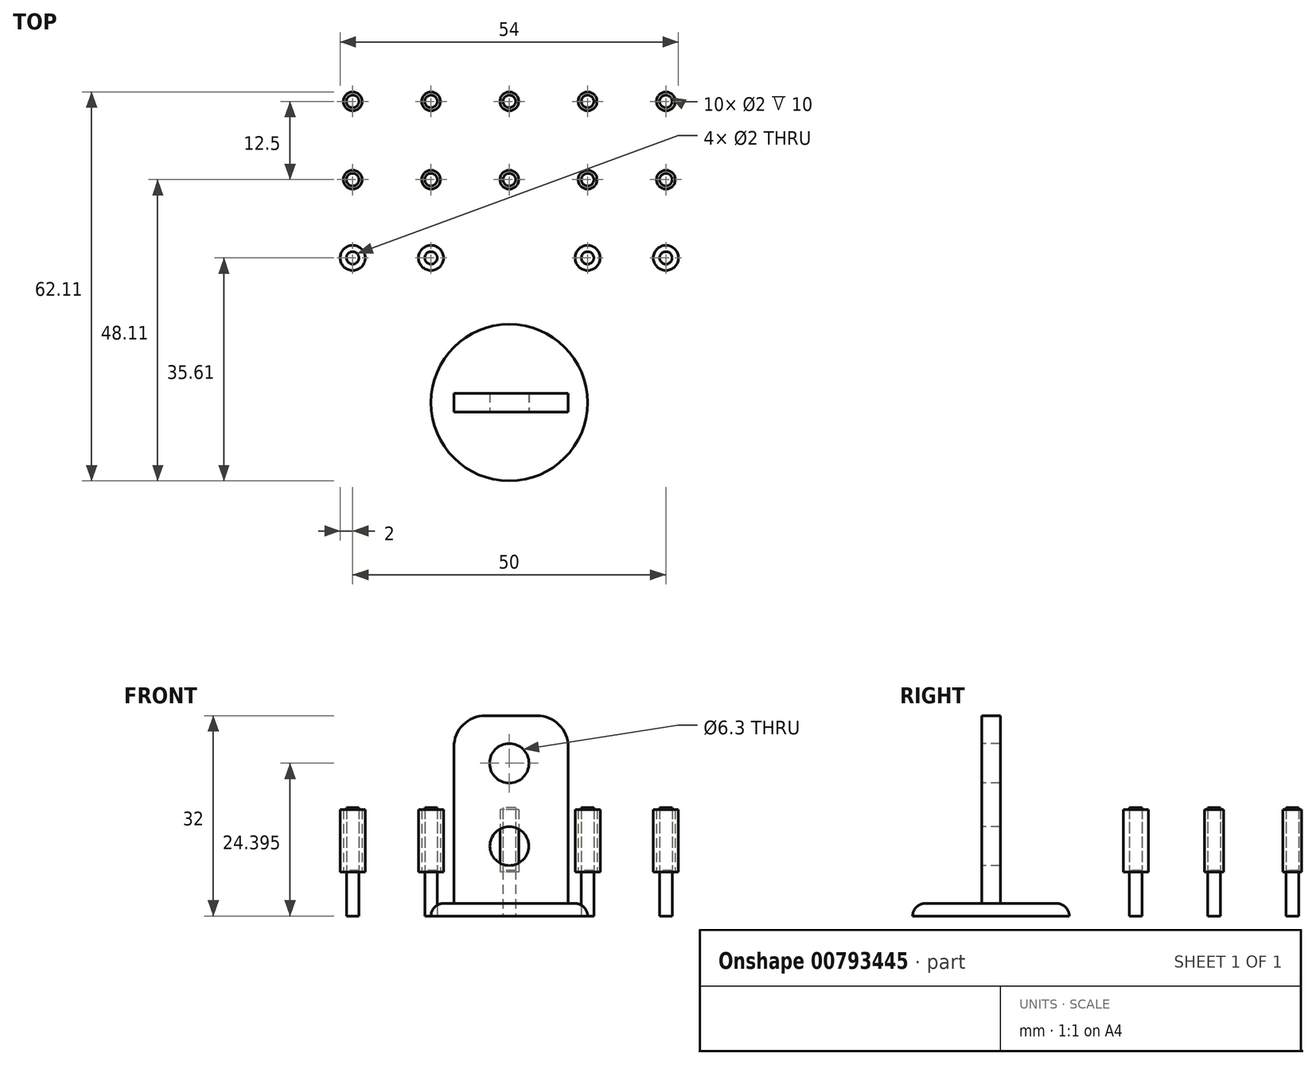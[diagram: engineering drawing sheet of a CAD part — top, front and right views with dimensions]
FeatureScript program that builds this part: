
annotation { "Feature Type Name" : "Feature", "Feature Type Description" : "" }
export const myFeature = defineFeature(function(context is Context, id is Id, definition is map)
    precondition{}
    {
        {
            var Q0;
            Q0=qCreatedBy(makeId("Top.planeOp"),FACE);
            var sketch = newSketch(context, id + "F0", { "sketchPlane" : qUnion([Q0])});
            skPoint(sketch, "E0.middle", {"position": v(0, 0) * mm});
            skCircle(sketch, "E1", {"center": v(-12.5, 25) * mm, "radius": 1 * mm});
            skCircle(sketch, "E2", {"center": v(0, 25) * mm, "radius": 1 * mm});
            skCircle(sketch, "E3", {"center": v(12.5, 25) * mm, "radius": 1 * mm});
            skCircle(sketch, "E4", {"center": v(25, 25) * mm, "radius": 1 * mm});
            skCircle(sketch, "E5", {"center": v(-25, 25) * mm, "radius": 1 * mm});
            skCircle(sketch, "E6", {"center": v(-25, 12.5) * mm, "radius": 1 * mm});
            skCircle(sketch, "E7", {"center": v(-12.5, 12.5) * mm, "radius": 1 * mm});
            skCircle(sketch, "E8", {"center": v(0, 12.5) * mm, "radius": 1 * mm});
            skCircle(sketch, "E9", {"center": v(12.5, 12.5) * mm, "radius": 1 * mm});
            skCircle(sketch, "E10", {"center": v(25, 12.5) * mm, "radius": 1 * mm});
            skCircle(sketch, "E11", {"center": v(-25, 0) * mm, "radius": 1 * mm});
            skCircle(sketch, "E12", {"center": v(-12.5, 0) * mm, "radius": 1 * mm});
            skCircle(sketch, "E13", {"center": v(12.5, 0) * mm, "radius": 1 * mm});
            skCircle(sketch, "E14", {"center": v(25, 0) * mm, "radius": 1 * mm});
            skSolve(sketch);
        }
        {
            var Q0;
            Q0=makeQuery(id+"F0.imprint","IMPRINT",FACE,{"disambiguationData":[TD([[makeQuery(id+"F0.imprint","IMPRINT",EDGE,{"derivedFrom":sQuery(id+"F0.wireOp",EDGE,"E5")}),1.0]])]});
            var Q1;
            Q1=makeQuery(id+"F0.imprint","IMPRINT",FACE,{"disambiguationData":[TD([[makeQuery(id+"F0.imprint","IMPRINT",EDGE,{"derivedFrom":sQuery(id+"F0.wireOp",EDGE,"E1")}),1.0]])]});
            var Q2;
            Q2=makeQuery(id+"F0.imprint","IMPRINT",FACE,{"disambiguationData":[TD([[makeQuery(id+"F0.imprint","IMPRINT",EDGE,{"derivedFrom":sQuery(id+"F0.wireOp",EDGE,"E6")}),1.0]])]});
            var Q3;
            Q3=makeQuery(id+"F0.imprint","IMPRINT",FACE,{"disambiguationData":[TD([[makeQuery(id+"F0.imprint","IMPRINT",EDGE,{"derivedFrom":sQuery(id+"F0.wireOp",EDGE,"E7")}),1.0]])]});
            var Q4;
            Q4=makeQuery(id+"F0.imprint","IMPRINT",FACE,{"disambiguationData":[TD([[makeQuery(id+"F0.imprint","IMPRINT",EDGE,{"derivedFrom":sQuery(id+"F0.wireOp",EDGE,"E2")}),1.0]])]});
            var Q5;
            Q5=makeQuery(id+"F0.imprint","IMPRINT",FACE,{"disambiguationData":[TD([[makeQuery(id+"F0.imprint","IMPRINT",EDGE,{"derivedFrom":sQuery(id+"F0.wireOp",EDGE,"E3")}),1.0]])]});
            var Q6;
            Q6=makeQuery(id+"F0.imprint","IMPRINT",FACE,{"disambiguationData":[TD([[makeQuery(id+"F0.imprint","IMPRINT",EDGE,{"derivedFrom":sQuery(id+"F0.wireOp",EDGE,"E8")}),1.0]])]});
            var Q7;
            Q7=makeQuery(id+"F0.imprint","IMPRINT",FACE,{"disambiguationData":[TD([[makeQuery(id+"F0.imprint","IMPRINT",EDGE,{"derivedFrom":sQuery(id+"F0.wireOp",EDGE,"E9")}),1.0]])]});
            var Q8;
            Q8=makeQuery(id+"F0.imprint","IMPRINT",FACE,{"disambiguationData":[TD([[makeQuery(id+"F0.imprint","IMPRINT",EDGE,{"derivedFrom":sQuery(id+"F0.wireOp",EDGE,"E4")}),1.0]])]});
            var Q9;
            Q9=makeQuery(id+"F0.imprint","IMPRINT",FACE,{"disambiguationData":[TD([[makeQuery(id+"F0.imprint","IMPRINT",EDGE,{"derivedFrom":sQuery(id+"F0.wireOp",EDGE,"E10")}),1.0]])]});
            var Q10;
            Q10=makeQuery(id+"F0.imprint","IMPRINT",FACE,{"disambiguationData":[TD([[makeQuery(id+"F0.imprint","IMPRINT",EDGE,{"derivedFrom":sQuery(id+"F0.wireOp",EDGE,"E14")}),1.0]])]});
            var Q11;
            Q11=makeQuery(id+"F0.imprint","IMPRINT",FACE,{"disambiguationData":[TD([[makeQuery(id+"F0.imprint","IMPRINT",EDGE,{"derivedFrom":sQuery(id+"F0.wireOp",EDGE,"E13")}),1.0]])]});
            var Q12;
            Q12=makeQuery(id+"F0.imprint","IMPRINT",FACE,{"disambiguationData":[TD([[makeQuery(id+"F0.imprint","IMPRINT",EDGE,{"derivedFrom":sQuery(id+"F0.wireOp",EDGE,"E12")}),1.0]])]});
            var Q13;
            Q13=makeQuery(id+"F0.imprint","IMPRINT",FACE,{"disambiguationData":[TD([[makeQuery(id+"F0.imprint","IMPRINT",EDGE,{"derivedFrom":sQuery(id+"F0.wireOp",EDGE,"E11")}),1.0]])]});
            extrude(context, id + "F1", {"entities" : qUnion([Q0, Q1, Q2, Q3, Q4, Q5, Q6, Q7, Q8, Q9, Q10, Q11, Q12, Q13]), "depth" : 7.3 * mm, "offsetDistance" : 25 * mm});
        }
        {
            var Q0;
            Q0=qCreatedBy(makeId("Top.planeOp"),FACE);
            cPlane(context, id + "F2", {"entities" : qUnion([Q0]), "cplaneType" : CPlaneType.OFFSET, "offset" : 7 * mm, "width" : 150 * mm, "height" : 150 * mm});
        }
        {
            var Q0;
            Q0=qCreatedBy(id+"F2.planeOp",FACE);
            var sketch = newSketch(context, id + "F3", { "sketchPlane" : qUnion([Q0])});
            skCircle(sketch, "E15.0.0", {"center": v(-25, 25) * mm, "radius": 1 * mm});
            skCircle(sketch, "E16.0.0", {"center": v(-12.5, 25) * mm, "radius": 1 * mm});
            skCircle(sketch, "E17.0.0", {"center": v(0, 25) * mm, "radius": 1 * mm});
            skCircle(sketch, "E18.0.0", {"center": v(-12.5, 12.5) * mm, "radius": 1 * mm});
            skCircle(sketch, "E19.0.0", {"center": v(-25, 12.5) * mm, "radius": 1 * mm});
            skCircle(sketch, "E20.0.0", {"center": v(0, 12.5) * mm, "radius": 1 * mm});
            skCircle(sketch, "E21.0.0", {"center": v(12.5, 25) * mm, "radius": 1 * mm});
            skCircle(sketch, "E22.0.0", {"center": v(12.5, 12.5) * mm, "radius": 1 * mm});
            skCircle(sketch, "E23.0.0", {"center": v(25, 12.5) * mm, "radius": 1 * mm});
            skCircle(sketch, "E24.0.0", {"center": v(25, 25) * mm, "radius": 1 * mm});
            skCircle(sketch, "E25.0.0", {"center": v(25, 0) * mm, "radius": 1 * mm});
            skCircle(sketch, "E26.0.0", {"center": v(12.5, 0) * mm, "radius": 1 * mm});
            skCircle(sketch, "E27.0.0", {"center": v(-12.5, 0) * mm, "radius": 1 * mm});
            skCircle(sketch, "E28.0.0", {"center": v(-25, 0) * mm, "radius": 1 * mm});
            skCircle(sketch, "E29", {"center": v(-25, 25) * mm, "radius": 1.5 * mm});
            skCircle(sketch, "E30", {"center": v(-12.5, 25) * mm, "radius": 1.5 * mm});
            skCircle(sketch, "E31", {"center": v(0, 25) * mm, "radius": 1.5 * mm});
            skCircle(sketch, "E32", {"center": v(12.5, 25) * mm, "radius": 1.5 * mm});
            skCircle(sketch, "E33", {"center": v(25, 25) * mm, "radius": 1.5 * mm});
            skCircle(sketch, "E34", {"center": v(-25, 12.5) * mm, "radius": 1.5 * mm});
            skCircle(sketch, "E35", {"center": v(-12.5, 12.5) * mm, "radius": 1.5 * mm});
            skCircle(sketch, "E36", {"center": v(0, 12.5) * mm, "radius": 1.5 * mm});
            skCircle(sketch, "E37", {"center": v(12.5, 12.5) * mm, "radius": 1.5 * mm});
            skCircle(sketch, "E38", {"center": v(25, 12.5) * mm, "radius": 1.5 * mm});
            skCircle(sketch, "E39", {"center": v(-25, 0) * mm, "radius": 2 * mm});
            skCircle(sketch, "E40", {"center": v(-12.5, 0) * mm, "radius": 2 * mm});
            skCircle(sketch, "E41", {"center": v(12.5, 0) * mm, "radius": 2 * mm});
            skCircle(sketch, "E42", {"center": v(25, 0) * mm, "radius": 2 * mm});
            skSolve(sketch);
        }
        {
            var Q0;
            Q0=makeQuery(id+"F3.imprint","IMPRINT",FACE,{"disambiguationData":[TD([[makeQuery(id+"F3.imprint","IMPRINT",EDGE,{"derivedFrom":sQuery(id+"F3.wireOp",EDGE,"E19.0.0")}),-1.0]])]});
            var Q1;
            Q1=makeQuery(id+"F1.opExtrude","CAP_FACE",FACE,{"disambiguationData":[OSD([sQuery(id+"F0.wireOp",EDGE,"E6")])],"isStart":false});
            var Q2;
            Q2=makeQuery(id+"F3.imprint","IMPRINT",FACE,{"disambiguationData":[TD([[makeQuery(id+"F3.imprint","IMPRINT",EDGE,{"derivedFrom":sQuery(id+"F3.wireOp",EDGE,"E28.0.0")}),-1.0]])]});
            var Q3;
            Q3=makeQuery(id+"F1.opExtrude","CAP_FACE",FACE,{"disambiguationData":[OSD([sQuery(id+"F0.wireOp",EDGE,"E11")])],"isStart":false});
            var Q4;
            Q4=makeQuery(id+"F3.imprint","IMPRINT",FACE,{"disambiguationData":[TD([[makeQuery(id+"F3.imprint","IMPRINT",EDGE,{"derivedFrom":sQuery(id+"F3.wireOp",EDGE,"E27.0.0")}),-1.0]])]});
            var Q5;
            Q5=makeQuery(id+"F1.opExtrude","CAP_FACE",FACE,{"disambiguationData":[OSD([sQuery(id+"F0.wireOp",EDGE,"E12")])],"isStart":false});
            var Q6;
            Q6=makeQuery(id+"F3.imprint","IMPRINT",FACE,{"disambiguationData":[TD([[makeQuery(id+"F3.imprint","IMPRINT",EDGE,{"derivedFrom":sQuery(id+"F3.wireOp",EDGE,"E18.0.0")}),-1.0]])]});
            var Q7;
            Q7=makeQuery(id+"F1.opExtrude","CAP_FACE",FACE,{"disambiguationData":[OSD([sQuery(id+"F0.wireOp",EDGE,"E7")])],"isStart":false});
            var Q8;
            Q8=makeQuery(id+"F3.imprint","IMPRINT",FACE,{"disambiguationData":[TD([[makeQuery(id+"F3.imprint","IMPRINT",EDGE,{"derivedFrom":sQuery(id+"F3.wireOp",EDGE,"E15.0.0")}),-1.0]])]});
            var Q9;
            Q9=makeQuery(id+"F1.opExtrude","CAP_FACE",FACE,{"disambiguationData":[OSD([sQuery(id+"F0.wireOp",EDGE,"E5")])],"isStart":false});
            var Q10;
            Q10=makeQuery(id+"F3.imprint","IMPRINT",FACE,{"disambiguationData":[TD([[makeQuery(id+"F3.imprint","IMPRINT",EDGE,{"derivedFrom":sQuery(id+"F3.wireOp",EDGE,"E16.0.0")}),-1.0]])]});
            var Q11;
            Q11=makeQuery(id+"F1.opExtrude","CAP_FACE",FACE,{"disambiguationData":[OSD([sQuery(id+"F0.wireOp",EDGE,"E1")])],"isStart":false});
            var Q12;
            Q12=makeQuery(id+"F3.imprint","IMPRINT",FACE,{"disambiguationData":[TD([[makeQuery(id+"F3.imprint","IMPRINT",EDGE,{"derivedFrom":sQuery(id+"F3.wireOp",EDGE,"E20.0.0")}),-1.0]])]});
            var Q13;
            Q13=makeQuery(id+"F1.opExtrude","CAP_FACE",FACE,{"disambiguationData":[OSD([sQuery(id+"F0.wireOp",EDGE,"E8")])],"isStart":false});
            var Q14;
            Q14=makeQuery(id+"F3.imprint","IMPRINT",FACE,{"disambiguationData":[TD([[makeQuery(id+"F3.imprint","IMPRINT",EDGE,{"derivedFrom":sQuery(id+"F3.wireOp",EDGE,"E17.0.0")}),-1.0]])]});
            var Q15;
            Q15=makeQuery(id+"F1.opExtrude","CAP_FACE",FACE,{"disambiguationData":[OSD([sQuery(id+"F0.wireOp",EDGE,"E2")])],"isStart":false});
            var Q16;
            Q16=makeQuery(id+"F3.imprint","IMPRINT",FACE,{"disambiguationData":[TD([[makeQuery(id+"F3.imprint","IMPRINT",EDGE,{"derivedFrom":sQuery(id+"F3.wireOp",EDGE,"E26.0.0")}),-1.0]])]});
            var Q17;
            Q17=makeQuery(id+"F1.opExtrude","CAP_FACE",FACE,{"disambiguationData":[OSD([sQuery(id+"F0.wireOp",EDGE,"E13")])],"isStart":false});
            var Q18;
            Q18=makeQuery(id+"F3.imprint","IMPRINT",FACE,{"disambiguationData":[TD([[makeQuery(id+"F3.imprint","IMPRINT",EDGE,{"derivedFrom":sQuery(id+"F3.wireOp",EDGE,"E22.0.0")}),-1.0]])]});
            var Q19;
            Q19=makeQuery(id+"F1.opExtrude","CAP_FACE",FACE,{"disambiguationData":[OSD([sQuery(id+"F0.wireOp",EDGE,"E9")])],"isStart":false});
            var Q20;
            Q20=makeQuery(id+"F3.imprint","IMPRINT",FACE,{"disambiguationData":[TD([[makeQuery(id+"F3.imprint","IMPRINT",EDGE,{"derivedFrom":sQuery(id+"F3.wireOp",EDGE,"E21.0.0")}),-1.0]])]});
            var Q21;
            Q21=makeQuery(id+"F1.opExtrude","CAP_FACE",FACE,{"disambiguationData":[OSD([sQuery(id+"F0.wireOp",EDGE,"E3")])],"isStart":false});
            var Q22;
            Q22=makeQuery(id+"F3.imprint","IMPRINT",FACE,{"disambiguationData":[TD([[makeQuery(id+"F3.imprint","IMPRINT",EDGE,{"derivedFrom":sQuery(id+"F3.wireOp",EDGE,"E24.0.0")}),-1.0]])]});
            var Q23;
            Q23=makeQuery(id+"F1.opExtrude","CAP_FACE",FACE,{"disambiguationData":[OSD([sQuery(id+"F0.wireOp",EDGE,"E4")])],"isStart":false});
            var Q24;
            Q24=makeQuery(id+"F3.imprint","IMPRINT",FACE,{"disambiguationData":[TD([[makeQuery(id+"F3.imprint","IMPRINT",EDGE,{"derivedFrom":sQuery(id+"F3.wireOp",EDGE,"E23.0.0")}),-1.0]])]});
            var Q25;
            Q25=makeQuery(id+"F1.opExtrude","CAP_FACE",FACE,{"disambiguationData":[OSD([sQuery(id+"F0.wireOp",EDGE,"E10")])],"isStart":false});
            var Q26;
            Q26=makeQuery(id+"F3.imprint","IMPRINT",FACE,{"disambiguationData":[TD([[makeQuery(id+"F3.imprint","IMPRINT",EDGE,{"derivedFrom":sQuery(id+"F3.wireOp",EDGE,"E25.0.0")}),-1.0]])]});
            var Q27;
            Q27=makeQuery(id+"F1.opExtrude","CAP_FACE",FACE,{"disambiguationData":[OSD([sQuery(id+"F0.wireOp",EDGE,"E14")])],"isStart":false});
            extrude(context, id + "F4", {"entities" : qUnion([Q0, Q1, Q2, Q3, Q4, Q5, Q6, Q7, Q8, Q9, Q10, Q11, Q12, Q13, Q14, Q15, Q16, Q17, Q18, Q19, Q20, Q21, Q22, Q23, Q24, Q25, Q26, Q27]), "depth" : 10 * mm, "offsetDistance" : 25 * mm});
        }
        {
            var Q0;
            Q0=qCreatedBy(makeId("Top.planeOp"),FACE);
            var sketch = newSketch(context, id + "F5", { "sketchPlane" : qUnion([Q0])});
            skCircle(sketch, "E43", {"center": v(0, -23.11) * mm, "radius": 12.5 * mm});
            skSolve(sketch);
        }
        {
            var Q0;
            Q0 = qSketchRegion(id + "F5", true);
            extrude(context, id + "F6", {"entities" : qUnion([Q0]), "depth" : 2 * mm, "offsetDistance" : 25 * mm});
        }
        {
            var Q0;
            Q0=makeQuery(id+"F6.opExtrude","CAP_FACE",FACE,{"disambiguationData":[OSD([sQuery(id+"F5.wireOp",EDGE,"E43")])],"isStart":false});
            var sketch = newSketch(context, id + "F7", { "sketchPlane" : qUnion([Q0])});
            skCircle(sketch, "E44.0.0", {"center": v(0, -23.11) * mm, "radius": 12.5 * mm, "construction": true});
            skLineSegment(sketch, "E45", {"start": v(0, -23.11) * mm, "end": v(12.5, -23.11) * mm, "construction": true});
            skLineSegment(sketch, "E46", {"start": v(12.5, -23.11) * mm, "end": v(-12.5, -23.11) * mm, "construction": true});
            skLineSegment(sketch, "E47", {"start": v(-8.84, -23.11) * mm, "end": v(-8.84, -21.61) * mm});
            skLineSegment(sketch, "E48", {"start": v(-8.84, -21.61) * mm, "end": v(9.4, -21.61) * mm});
            skLineSegment(sketch, "E49", {"start": v(9.4, -21.61) * mm, "end": v(9.4, -23.11) * mm});
            skLineSegment(sketch, "E50.MirrorCS", {"start": v(-8.84, -23.11) * mm, "end": v(-8.84, -24.61) * mm});
            skLineSegment(sketch, "E51.MirrorCS", {"start": v(-8.84, -24.61) * mm, "end": v(9.4, -24.61) * mm});
            skLineSegment(sketch, "E52.MirrorCS", {"start": v(9.4, -24.61) * mm, "end": v(9.4, -23.11) * mm});
            skSolve(sketch);
        }
        {
            var Q0;
            Q0 = qSketchRegion(id + "F7", true);
            extrude(context, id + "F8", {"entities" : qUnion([Q0]), "operationType" : NewBodyOperationType.ADD, "depth" : 30 * mm, "offsetDistance" : 25 * mm});
        }
        {
            var Q0;
            Q0=makeQuery(id+"F8.opExtrude","SWEPT_FACE",FACE,{"disambiguationData":[OSD([sQuery(id+"F7.wireOp",EDGE,"E51.MirrorCS")])]});
            cPlane(context, id + "F9", {"entities" : qUnion([Q0]), "cplaneType" : CPlaneType.OFFSET, "offset" : 0 * mm, "width" : 150 * mm, "height" : 150 * mm});
        }
        {
            var Q0;
            Q0=qCreatedBy(id+"F9.planeOp",FACE);
            var sketch = newSketch(context, id + "F10", { "sketchPlane" : qUnion([Q0])});
            skCircle(sketch, "E53", {"center": v(0, 24.4) * mm, "radius": 3.15 * mm});
            skCircle(sketch, "E54", {"center": v(0, 11.16) * mm, "radius": 3.1 * mm});
            skSolve(sketch);
        }
        {
            var Q0;
            Q0 = qSketchRegion(id + "F10", true);
            extrude(context, id + "F11", {"entities" : qUnion([Q0]), "operationType" : NewBodyOperationType.REMOVE, "oppositeDirection" : true, "depth" : 7.8 * mm, "offsetDistance" : 25 * mm});
        }
        {
            var Q0;
            Q0=makeQuery(id+"F8.opExtrude","CAP_EDGE",EDGE,{"disambiguationData":[OSD([sQuery(id+"F7.wireOp",EDGE,"E49"),sQuery(id+"F7.wireOp",EDGE,"E52.MirrorCS")])],"isStart":false});
            var Q1;
            Q1=makeQuery(id+"F8.opExtrude","CAP_EDGE",EDGE,{"disambiguationData":[OSD([sQuery(id+"F7.wireOp",EDGE,"E47"),sQuery(id+"F7.wireOp",EDGE,"E50.MirrorCS")])],"isStart":false});
            fillet(context, id + "F12", {"entities" : qUnion([Q0, Q1]), "radius" : 5 * mm, "tangentPropagation" : true, "allowEdgeOverflow" : false});
        }
        {
            var Q0;
            Q0=makeQuery(id+"F6.opExtrude","CAP_EDGE",EDGE,{"disambiguationData":[OSD([sQuery(id+"F5.wireOp",EDGE,"E43")])],"isStart":false});
            fillet(context, id + "F13", {"entities" : qUnion([Q0]), "radius" : 2 * mm, "tangentPropagation" : true, "allowEdgeOverflow" : false});
        }
    });
